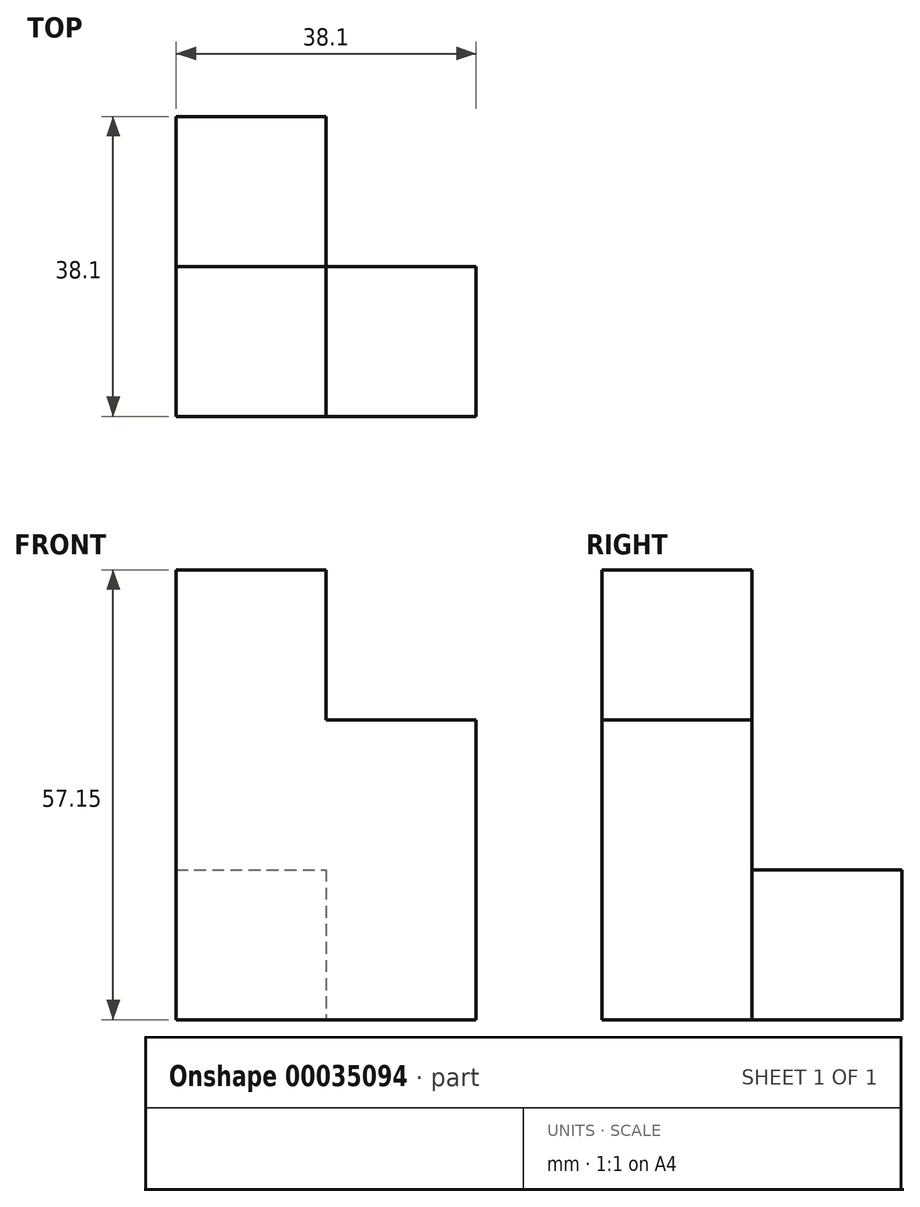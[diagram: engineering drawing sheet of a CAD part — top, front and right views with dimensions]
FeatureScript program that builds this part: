
annotation { "Feature Type Name" : "Feature", "Feature Type Description" : "" }
export const myFeature = defineFeature(function(context is Context, id is Id, definition is map)
    precondition{}
    {
        {
            var Q0;
            Q0=qCreatedBy(makeId("Front.planeOp"),FACE);
            var sketch = newSketch(context, id + "F0", { "sketchPlane" : qUnion([Q0])});
            skLineSegment(sketch, "E0", {"start": v(-75.16, 44.56) * mm, "end": v(-56.11, 44.56) * mm});
            skLineSegment(sketch, "E1", {"start": v(-56.11, 44.56) * mm, "end": v(-56.11, 6.46) * mm});
            skLineSegment(sketch, "E2", {"start": v(-56.11, 6.46) * mm, "end": v(-37.06, 6.46) * mm});
            skLineSegment(sketch, "E3", {"start": v(-37.06, 6.46) * mm, "end": v(-37.06, -12.59) * mm});
            skLineSegment(sketch, "E4", {"start": v(-37.06, -12.59) * mm, "end": v(-75.16, -12.59) * mm});
            skLineSegment(sketch, "E5", {"start": v(-75.16, -12.59) * mm, "end": v(-75.16, 44.56) * mm});
            skSolve(sketch);
        }
        {
            var Q0;
            Q0 = qSketchRegion(id + "F0", true);
            extrude(context, id + "F1", {"entities" : qUnion([Q0]), "depth" : 19.05 * mm});
        }
        {
            var Q0;
            Q0=makeQuery(id+"F1.opExtrude","SWEPT_FACE",FACE,{"disambiguationData":[OSD([sQuery(id+"F0.wireOp",EDGE,"E1")])]});
            var sketch = newSketch(context, id + "F2", { "sketchPlane" : qUnion([Q0])});
            skLineSegment(sketch, "E6", {"start": v(-19.05, 25.51) * mm, "end": v(0, 25.51) * mm});
            skLineSegment(sketch, "E7", {"start": v(0, 25.51) * mm, "end": v(0, 6.46) * mm});
            skLineSegment(sketch, "E8", {"start": v(0, 6.46) * mm, "end": v(-19.05, 6.46) * mm});
            skLineSegment(sketch, "E9", {"start": v(-19.05, 6.46) * mm, "end": v(-19.05, 25.51) * mm});
            skSolve(sketch);
        }
        {
            var Q0;
            Q0 = qSketchRegion(id + "F2", true);
            extrude(context, id + "F3", {"entities" : qUnion([Q0]), "operationType" : NewBodyOperationType.ADD, "depth" : 19.05 * mm});
        }
        {
            var Q0;
            Q0=makeQuery(id+"F3.boolean.opBoolean","MERGE",FACE,{"derivedFrom":[makeQuery(id+"F1.opExtrude","CAP_FACE",FACE,{"disambiguationData":[OSD([sQuery(id+"F0.wireOp",EDGE,"E0"),sQuery(id+"F0.wireOp",EDGE,"E1"),sQuery(id+"F0.wireOp",EDGE,"E2"),sQuery(id+"F0.wireOp",EDGE,"E3"),sQuery(id+"F0.wireOp",EDGE,"E4"),sQuery(id+"F0.wireOp",EDGE,"E5")])],"isStart":true}),makeQuery(id+"F3.opExtrude","SWEPT_FACE",FACE,{"disambiguationData":[OSD([sQuery(id+"F2.wireOp",EDGE,"E7")])]})]});
            var sketch = newSketch(context, id + "F4", { "sketchPlane" : qUnion([Q0])});
            skLineSegment(sketch, "E10", {"start": v(75.16, 6.46) * mm, "end": v(56.11, 6.46) * mm});
            skLineSegment(sketch, "E11", {"start": v(56.11, 6.46) * mm, "end": v(56.11, -12.59) * mm});
            skLineSegment(sketch, "E12", {"start": v(56.11, -12.59) * mm, "end": v(75.16, -12.59) * mm});
            skLineSegment(sketch, "E13", {"start": v(75.16, -12.59) * mm, "end": v(75.16, 6.46) * mm});
            skSolve(sketch);
        }
        {
            var Q0;
            Q0 = qSketchRegion(id + "F4", true);
            extrude(context, id + "F5", {"entities" : qUnion([Q0]), "operationType" : NewBodyOperationType.ADD, "depth" : 19.05 * mm});
        }
    });
